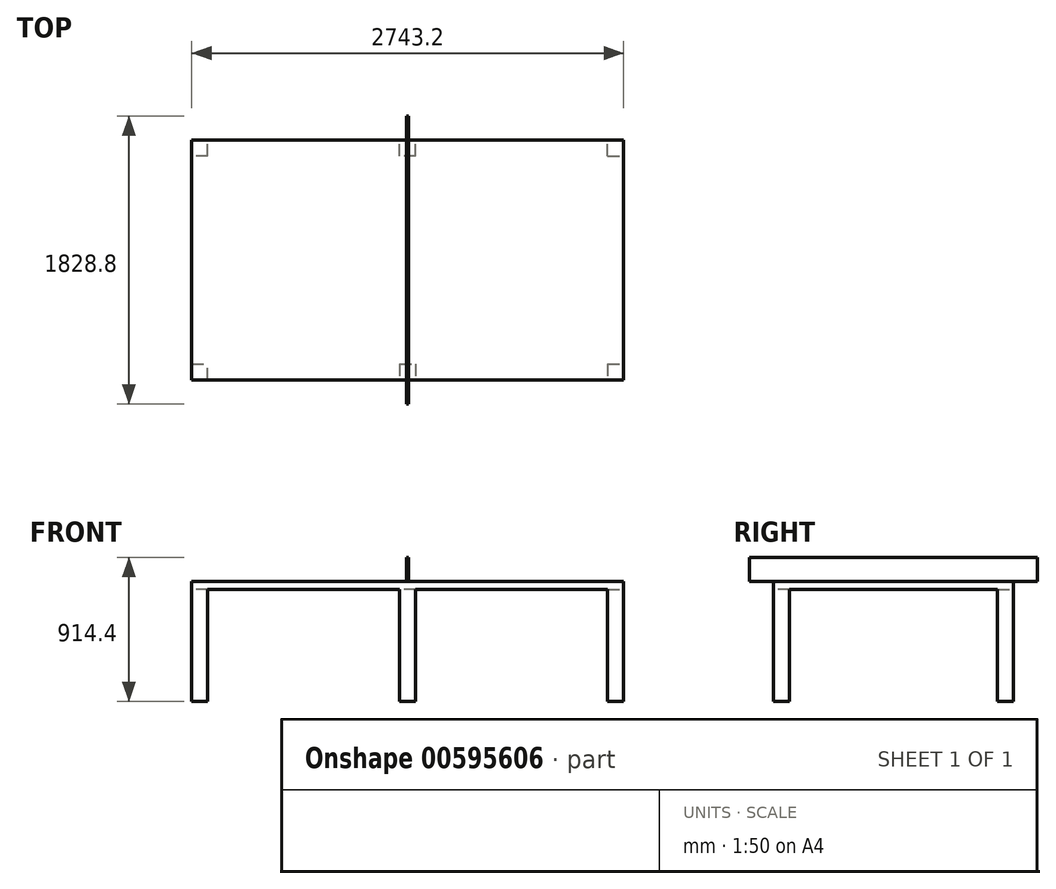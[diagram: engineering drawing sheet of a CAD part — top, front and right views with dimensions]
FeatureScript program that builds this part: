
annotation { "Feature Type Name" : "Feature", "Feature Type Description" : "" }
export const myFeature = defineFeature(function(context is Context, id is Id, definition is map)
    precondition{}
    {
        {
            var Q0;
            Q0=qCreatedBy(makeId("Top.planeOp"),FACE);
            var sketch = newSketch(context, id + "F0", { "sketchPlane" : qUnion([Q0])});
            skLineSegment(sketch, "E0.bottom", {"start": v(-1371.45, -210.78) * mm, "end": v(1371.75, -210.78) * mm});
            skLineSegment(sketch, "E0.top", {"start": v(-1371.45, -1734.78) * mm, "end": v(1371.75, -1734.78) * mm});
            skLineSegment(sketch, "E0.left", {"start": v(-1371.45, -210.78) * mm, "end": v(-1371.45, -1734.78) * mm});
            skLineSegment(sketch, "E0.right", {"start": v(1371.75, -210.78) * mm, "end": v(1371.75, -1734.78) * mm});
            skSolve(sketch);
        }
        {
            var Q0;
            Q0=makeQuery(id+"F0.imprint","IMPRINT",FACE,{"disambiguationData":[TD([[makeQuery(id+"F0.imprint","IMPRINT",EDGE,{"derivedFrom":sQuery(id+"F0.wireOp",EDGE,"E0.bottom")}),-1.0]])]});
            extrude(context, id + "F1", {"entities" : qUnion([Q0]), "depth" : 50.8 * mm, "offsetDistance" : 25.4 * mm});
        }
        {
            var Q0;
            Q0=makeQuery(id+"F1.opExtrude","CAP_FACE",FACE,{"disambiguationData":[OSD([sQuery(id+"F0.wireOp",EDGE,"E0.bottom"),sQuery(id+"F0.wireOp",EDGE,"E0.top"),sQuery(id+"F0.wireOp",EDGE,"E0.left"),sQuery(id+"F0.wireOp",EDGE,"E0.right")])],"isStart":false});
            var sketch = newSketch(context, id + "F2", { "sketchPlane" : qUnion([Q0])});
            skLineSegment(sketch, "E1", {"start": v(0.15, -210.78) * mm, "end": v(0.15, -1734.78) * mm, "construction": true});
            skLineSegment(sketch, "E2.bottom", {"start": v(-6.2, -58.38) * mm, "end": v(6.5, -58.38) * mm});
            skLineSegment(sketch, "E2.top", {"start": v(-6.2, -1887.18) * mm, "end": v(6.5, -1887.18) * mm});
            skLineSegment(sketch, "E2.left", {"start": v(-6.2, -58.38) * mm, "end": v(-6.2, -1887.18) * mm});
            skLineSegment(sketch, "E2.right", {"start": v(6.5, -58.38) * mm, "end": v(6.5, -1887.18) * mm});
            skSolve(sketch);
        }
        {
            var Q0;
            {var subQ0=sQuery(id+"F2.wireOp",EDGE,"E2.left");var subQ1=makeQuery(id+"F1.opExtrude","CAP_EDGE",EDGE,{"disambiguationData":[OSD([sQuery(id+"F0.wireOp",EDGE,"E0.bottom")])],"isStart":false});var subQ2=makeQuery(id+"F2.imprint","INTERSECT",VERTEX,{"derivedFrom":[subQ1,subQ0]});Q0=makeQuery(id+"F2.imprint","IMPRINT",FACE,{"disambiguationData":[TD([[makeQuery(id+"F2.imprint","IMPRINT",EDGE,{"disambiguationData":[TD([[subQ2,-1.0]])],"derivedFrom":subQ0}),1.0]])]});}
            var Q1;
            {var subQ0=sQuery(id+"F2.wireOp",EDGE,"E2.top");Q1=makeQuery(id+"F2.imprint","IMPRINT",FACE,{"disambiguationData":[TD([[makeQuery(id+"F2.imprint","IMPRINT",EDGE,{"derivedFrom":subQ0}),1.0]])]});}
            var Q2;
            {var subQ0=sQuery(id+"F2.wireOp",EDGE,"E2.bottom");Q2=makeQuery(id+"F2.imprint","IMPRINT",FACE,{"disambiguationData":[TD([[makeQuery(id+"F2.imprint","IMPRINT",EDGE,{"derivedFrom":subQ0}),-1.0]])]});}
            extrude(context, id + "F3", {"entities" : qUnion([Q0, Q1, Q2]), "depth" : 152.4 * mm, "offsetDistance" : 25.4 * mm});
        }
        {
            var Q0;
            Q0=makeQuery(id+"F1.opExtrude","CAP_FACE",FACE,{"disambiguationData":[OSD([sQuery(id+"F0.wireOp",EDGE,"E0.bottom"),sQuery(id+"F0.wireOp",EDGE,"E0.top"),sQuery(id+"F0.wireOp",EDGE,"E0.left"),sQuery(id+"F0.wireOp",EDGE,"E0.right")])],"isStart":true});
            var sketch = newSketch(context, id + "F4", { "sketchPlane" : qUnion([Q0])});
            skLineSegment(sketch, "E3.bottom", {"start": v(-1371.45, 1734.78) * mm, "end": v(-1269.85, 1734.78) * mm});
            skLineSegment(sketch, "E3.top", {"start": v(-1371.45, 1633.18) * mm, "end": v(-1269.85, 1633.18) * mm});
            skLineSegment(sketch, "E3.left", {"start": v(-1371.45, 1734.78) * mm, "end": v(-1371.45, 1633.18) * mm});
            skLineSegment(sketch, "E3.right", {"start": v(-1269.85, 1734.78) * mm, "end": v(-1269.85, 1633.18) * mm});
            skLineSegment(sketch, "E4.bottom", {"start": v(-50.65, 1633.18) * mm, "end": v(50.95, 1633.18) * mm});
            skLineSegment(sketch, "E4.top", {"start": v(-50.65, 1734.78) * mm, "end": v(50.95, 1734.78) * mm});
            skLineSegment(sketch, "E4.left", {"start": v(-50.65, 1633.18) * mm, "end": v(-50.65, 1734.78) * mm});
            skLineSegment(sketch, "E4.right", {"start": v(50.95, 1633.18) * mm, "end": v(50.95, 1734.78) * mm});
            skLineSegment(sketch, "E5.bottom", {"start": v(1270.15, 1633.18) * mm, "end": v(1371.75, 1633.18) * mm});
            skLineSegment(sketch, "E5.top", {"start": v(1270.15, 1734.78) * mm, "end": v(1371.75, 1734.78) * mm});
            skLineSegment(sketch, "E5.left", {"start": v(1270.15, 1633.18) * mm, "end": v(1270.15, 1734.78) * mm});
            skLineSegment(sketch, "E5.right", {"start": v(1371.75, 1633.18) * mm, "end": v(1371.75, 1734.78) * mm});
            skLineSegment(sketch, "E6.bottom", {"start": v(1270.15, 312.38) * mm, "end": v(1371.75, 312.38) * mm});
            skLineSegment(sketch, "E6.top", {"start": v(1270.15, 210.78) * mm, "end": v(1371.75, 210.78) * mm});
            skLineSegment(sketch, "E6.left", {"start": v(1270.15, 312.38) * mm, "end": v(1270.15, 210.78) * mm});
            skLineSegment(sketch, "E6.right", {"start": v(1371.75, 312.38) * mm, "end": v(1371.75, 210.78) * mm});
            skLineSegment(sketch, "E7.bottom", {"start": v(50.95, 312.38) * mm, "end": v(-50.65, 312.38) * mm});
            skLineSegment(sketch, "E7.top", {"start": v(50.95, 210.78) * mm, "end": v(-50.65, 210.78) * mm});
            skLineSegment(sketch, "E7.left", {"start": v(50.95, 312.38) * mm, "end": v(50.95, 210.78) * mm});
            skLineSegment(sketch, "E7.right", {"start": v(-50.65, 312.38) * mm, "end": v(-50.65, 210.78) * mm});
            skLineSegment(sketch, "E8.bottom", {"start": v(-1269.85, 312.38) * mm, "end": v(-1371.45, 312.38) * mm});
            skLineSegment(sketch, "E8.top", {"start": v(-1269.85, 210.78) * mm, "end": v(-1371.45, 210.78) * mm});
            skLineSegment(sketch, "E8.left", {"start": v(-1269.85, 312.38) * mm, "end": v(-1269.85, 210.78) * mm});
            skLineSegment(sketch, "E8.right", {"start": v(-1371.45, 312.38) * mm, "end": v(-1371.45, 210.78) * mm});
            skSolve(sketch);
        }
        {
            var Q0;
            Q0 = qSketchRegion(id + "F4", true);
            extrude(context, id + "F5", {"entities" : qUnion([Q0]), "operationType" : NewBodyOperationType.ADD, "depth" : 711.2 * mm, "offsetDistance" : 25.4 * mm});
        }
    });
